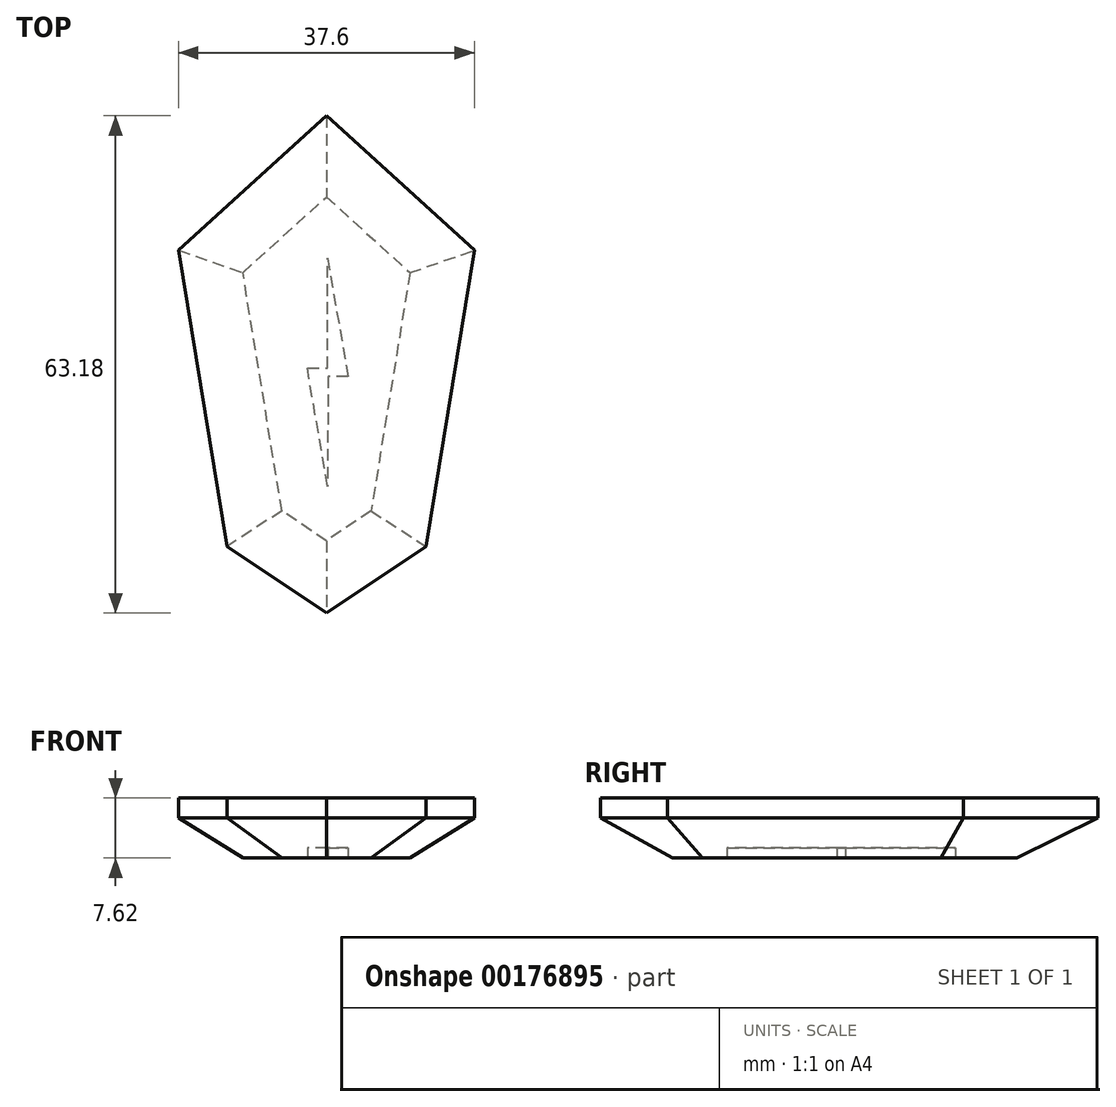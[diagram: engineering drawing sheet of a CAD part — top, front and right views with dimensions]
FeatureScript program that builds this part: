
annotation { "Feature Type Name" : "Feature", "Feature Type Description" : "" }
export const myFeature = defineFeature(function(context is Context, id is Id, definition is map)
    precondition{}
    {
        {
            var Q0;
            Q0=qCreatedBy(makeId("Top.planeOp"),FACE);
            var sketch = newSketch(context, id + "F0", { "sketchPlane" : qUnion([Q0])});
            skLineSegment(sketch, "E0.bottom", {"start": v(-7.62, 13.79) * mm, "end": v(10.16, 13.79) * mm});
            skLineSegment(sketch, "E0.top", {"start": v(-7.62, -18.15) * mm, "end": v(10.16, -18.15) * mm});
            skLineSegment(sketch, "E0.left", {"start": v(-7.62, 13.79) * mm, "end": v(-7.62, -18.15) * mm});
            skLineSegment(sketch, "E0.right", {"start": v(10.16, 13.79) * mm, "end": v(10.16, -18.15) * mm});
            skLineSegment(sketch, "E1", {"start": v(10.16, 13.79) * mm, "end": v(20.07, 16.03) * mm});
            skLineSegment(sketch, "E2", {"start": v(-7.62, 13.79) * mm, "end": v(-17.53, 16.03) * mm});
            skLineSegment(sketch, "E3", {"start": v(20.07, 16.03) * mm, "end": v(1.27, 33.11) * mm});
            skLineSegment(sketch, "E4", {"start": v(-17.53, 16.03) * mm, "end": v(1.27, 33.11) * mm});
            skLineSegment(sketch, "E5", {"start": v(-7.62, -18.15) * mm, "end": v(-11.38, -21.57) * mm});
            skLineSegment(sketch, "E6", {"start": v(10.16, -18.15) * mm, "end": v(13.92, -21.57) * mm});
            skLineSegment(sketch, "E7", {"start": v(-17.53, 16.03) * mm, "end": v(-11.38, -21.57) * mm});
            skLineSegment(sketch, "E8", {"start": v(20.07, 16.03) * mm, "end": v(13.92, -21.57) * mm});
            skLineSegment(sketch, "E9", {"start": v(-11.38, -21.57) * mm, "end": v(1.27, -30.07) * mm});
            skLineSegment(sketch, "E10", {"start": v(1.27, -30.07) * mm, "end": v(13.92, -21.57) * mm});
            skSolve(sketch);
        }
        {
            var Q0;
            Q0=makeQuery(id+"F0.imprint","IMPRINT",FACE,{"disambiguationData":[TD([[makeQuery(id+"F0.imprint","IMPRINT",EDGE,{"derivedFrom":sQuery(id+"F0.wireOp",EDGE,"E0.bottom")}),-1.0]])]});
            var Q1;
            Q1=makeQuery(id+"F0.imprint","IMPRINT",FACE,{"disambiguationData":[TD([[makeQuery(id+"F0.imprint","IMPRINT",EDGE,{"derivedFrom":sQuery(id+"F0.wireOp",EDGE,"E0.right")}),1.0]])]});
            var Q2;
            Q2=makeQuery(id+"F0.imprint","IMPRINT",FACE,{"disambiguationData":[TD([[makeQuery(id+"F0.imprint","IMPRINT",EDGE,{"derivedFrom":sQuery(id+"F0.wireOp",EDGE,"E0.left")}),-1.0]])]});
            var Q3;
            Q3=makeQuery(id+"F0.imprint","IMPRINT",FACE,{"disambiguationData":[TD([[makeQuery(id+"F0.imprint","IMPRINT",EDGE,{"derivedFrom":sQuery(id+"F0.wireOp",EDGE,"E0.top")}),-1.0]])]});
            var Q4;
            Q4=makeQuery(id+"F0.imprint","IMPRINT",FACE,{"disambiguationData":[TD([[makeQuery(id+"F0.imprint","IMPRINT",EDGE,{"derivedFrom":sQuery(id+"F0.wireOp",EDGE,"E0.bottom")}),1.0]])]});
            extrude(context, id + "F1", {"entities" : qUnion([Q0, Q1, Q2, Q3, Q4]), "depth" : 7.62 * mm});
        }
        {
            var Q0;
            Q0=makeQuery(id+"F1.opExtrude","CAP_FACE",FACE,{"disambiguationData":[OSD([sQuery(id+"F0.wireOp",EDGE,"E3"),sQuery(id+"F0.wireOp",EDGE,"E4"),sQuery(id+"F0.wireOp",EDGE,"E7"),sQuery(id+"F0.wireOp",EDGE,"E8"),sQuery(id+"F0.wireOp",EDGE,"E9"),sQuery(id+"F0.wireOp",EDGE,"E10")])],"isStart":true});
            chamfer(context, id + "F2", {"entities" : qUnion([Q0]), "chamferType" : ChamferType.TWO_OFFSETS, "width1" : 5.08 * mm, "oppositeDirection" : false, "width2" : 7.62 * mm, "tangentPropagation" : true});
        }
        {
            var Q0;
            Q0=makeQuery(id+"F1.opExtrude","CAP_FACE",FACE,{"disambiguationData":[OSD([sQuery(id+"F0.wireOp",EDGE,"E3"),sQuery(id+"F0.wireOp",EDGE,"E4"),sQuery(id+"F0.wireOp",EDGE,"E7"),sQuery(id+"F0.wireOp",EDGE,"E8"),sQuery(id+"F0.wireOp",EDGE,"E9"),sQuery(id+"F0.wireOp",EDGE,"E10")])],"isStart":true});
            var sketch = newSketch(context, id + "F3", { "sketchPlane" : qUnion([Q0])});
            skLineSegment(sketch, "E11", {"start": v(1.39, -15) * mm, "end": v(4.03, 0) * mm});
            skLineSegment(sketch, "E12", {"start": v(4.03, 0) * mm, "end": v(1.49, 0) * mm});
            skLineSegment(sketch, "E13", {"start": v(1.49, 0) * mm, "end": v(1.39, 13.97) * mm});
            skLineSegment(sketch, "E14", {"start": v(1.39, 13.97) * mm, "end": v(-1.15, -1.06) * mm});
            skLineSegment(sketch, "E15", {"start": v(-1.15, -1.06) * mm, "end": v(1.39, -1.04) * mm});
            skLineSegment(sketch, "E16", {"start": v(1.39, -1.04) * mm, "end": v(1.39, -15) * mm});
            skSolve(sketch);
        }
        {
            var Q0;
            Q0=makeQuery(id+"F3.imprint","IMPRINT",FACE,{"disambiguationData":[TD([[makeQuery(id+"F3.imprint","IMPRINT",EDGE,{"derivedFrom":sQuery(id+"F3.wireOp",EDGE,"E11")}),1.0]])]});
            extrude(context, id + "F4", {"entities" : qUnion([Q0]), "operationType" : NewBodyOperationType.REMOVE, "oppositeDirection" : true, "depth" : 1.27 * mm});
        }
    });
